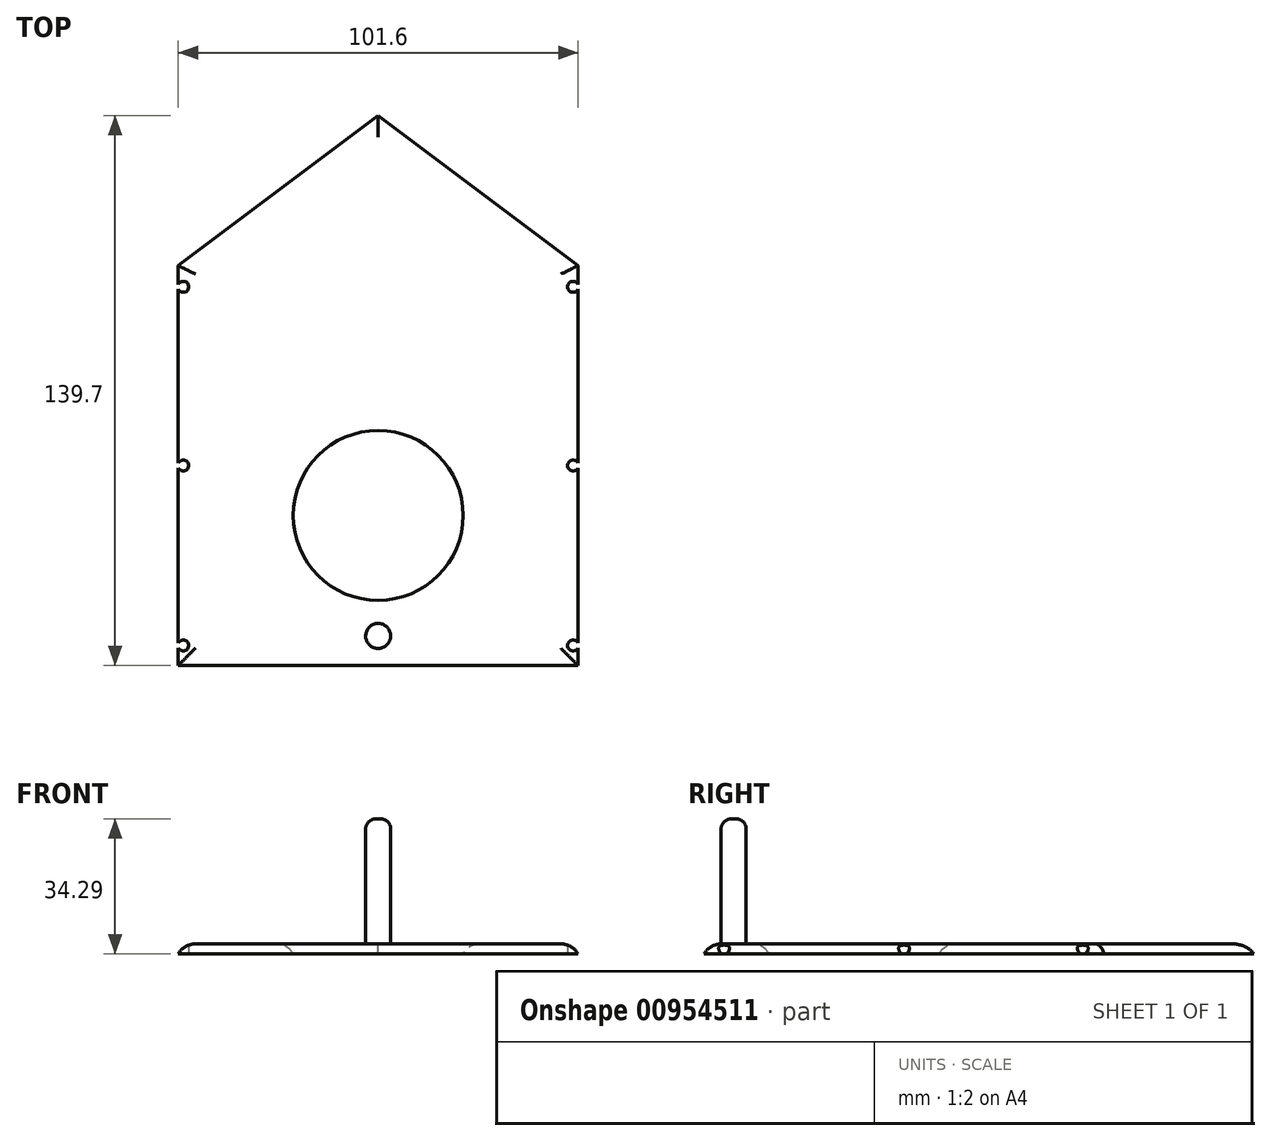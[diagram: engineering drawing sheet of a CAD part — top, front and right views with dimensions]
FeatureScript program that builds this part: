
annotation { "Feature Type Name" : "Feature", "Feature Type Description" : "" }
export const myFeature = defineFeature(function(context is Context, id is Id, definition is map)
    precondition{}
    {
        {
            var Q0;
            Q0=qCreatedBy(makeId("Top.planeOp"),FACE);
            var sketch = newSketch(context, id + "F0", { "sketchPlane" : qUnion([Q0])});
            skLineSegment(sketch, "E0.bottom", {"start": v(50.8, -50.8) * mm, "end": v(-50.8, -50.8) * mm});
            skLineSegment(sketch, "E0.top", {"start": v(50.8, 50.8) * mm, "end": v(-50.8, 50.8) * mm});
            skLineSegment(sketch, "E0.left", {"start": v(50.8, -50.8) * mm, "end": v(50.8, 50.8) * mm});
            skLineSegment(sketch, "E0.right", {"start": v(-50.8, -50.8) * mm, "end": v(-50.8, 50.8) * mm});
            skPoint(sketch, "E0.middle", {"position": v(0, 0) * mm});
            skLineSegment(sketch, "E1", {"start": v(-50.8, 50.8) * mm, "end": v(0, 88.9) * mm});
            skLineSegment(sketch, "E2", {"start": v(0, 88.9) * mm, "end": v(50.8, 50.8) * mm});
            skPoint(sketch, "E3", {"position": v(0, -12.7) * mm});
            skCircle(sketch, "E4", {"center": v(0, -12.7) * mm, "radius": 21.59 * mm});
            skSolve(sketch);
        }
        {
            var Q0;
            Q0 = qSketchRegion(id + "F0", true);
            extrude(context, id + "F1", {"entities" : qUnion([Q0]), "depth" : 2.54 * mm, "offsetDistance" : 25.4 * mm});
        }
        {
            var Q0;
            Q0=makeQuery(id+"F1.opExtrude","CAP_EDGE",EDGE,{"disambiguationData":[OSD([sQuery(id+"F0.wireOp",EDGE,"E4")])],"isStart":false});
            fillet(context, id + "F2", {"entities" : qUnion([Q0]), "radius" : 4.83 * mm, "tangentPropagation" : true, "allowEdgeOverflow" : false});
        }
        {
            var Q0;
            Q0=makeQuery(id+"F1.opExtrude","CAP_FACE",FACE,{"disambiguationData":[OSD([sQuery(id+"F0.wireOp",EDGE,"E0.bottom"),sQuery(id+"F0.wireOp",EDGE,"E0.left"),sQuery(id+"F0.wireOp",EDGE,"E0.right"),sQuery(id+"F0.wireOp",EDGE,"E1"),sQuery(id+"F0.wireOp",EDGE,"E2"),sQuery(id+"F0.wireOp",EDGE,"E4")])],"isStart":false});
            var sketch = newSketch(context, id + "F3", { "sketchPlane" : qUnion([Q0])});
            skPoint(sketch, "E5", {"position": v(0, -43.3) * mm});
            skCircle(sketch, "E6", {"center": v(0, -43.3) * mm, "radius": 3.18 * mm});
            skSolve(sketch);
        }
        {
            var Q0;
            Q0=makeQuery(id+"F3.imprint","IMPRINT",FACE,{"disambiguationData":[TD([[makeQuery(id+"F3.imprint","IMPRINT",EDGE,{"derivedFrom":sQuery(id+"F3.wireOp",EDGE,"E6")}),1.0]])]});
            extrude(context, id + "F4", {"entities" : qUnion([Q0]), "operationType" : NewBodyOperationType.ADD, "depth" : 31.75 * mm, "offsetDistance" : 25.4 * mm});
        }
        {
            var Q0;
            Q0=makeQuery(id+"F4.opExtrude","CAP_EDGE",EDGE,{"disambiguationData":[OSD([sQuery(id+"F3.wireOp",EDGE,"E6")])],"isStart":false});
            fillet(context, id + "F5", {"entities" : qUnion([Q0]), "radius" : 2.54 * mm, "tangentPropagation" : true, "allowEdgeOverflow" : false});
        }
        {
            var Q0;
            Q0=makeQuery(id+"F1.opExtrude","CAP_EDGE",EDGE,{"disambiguationData":[OSD([sQuery(id+"F0.wireOp",EDGE,"E0.bottom")])],"isStart":false});
            var Q1;
            Q1=makeQuery(id+"F1.opExtrude","CAP_EDGE",EDGE,{"disambiguationData":[OSD([sQuery(id+"F0.wireOp",EDGE,"E0.left")])],"isStart":false});
            var Q2;
            Q2=makeQuery(id+"F1.opExtrude","CAP_EDGE",EDGE,{"disambiguationData":[OSD([sQuery(id+"F0.wireOp",EDGE,"E0.right")])],"isStart":false});
            var Q3;
            Q3=makeQuery(id+"F1.opExtrude","CAP_EDGE",EDGE,{"disambiguationData":[OSD([sQuery(id+"F0.wireOp",EDGE,"E1")])],"isStart":false});
            var Q4;
            Q4=makeQuery(id+"F1.opExtrude","CAP_EDGE",EDGE,{"disambiguationData":[OSD([sQuery(id+"F0.wireOp",EDGE,"E2")])],"isStart":false});
            fillet(context, id + "F6", {"entities" : qUnion([Q0, Q1, Q2, Q3, Q4]), "radius" : 5.08 * mm, "tangentPropagation" : true, "allowEdgeOverflow" : false});
        }
        {
            var Q0;
            Q0=makeQuery(id+"F0.imprint","IMPRINT",FACE,{"disambiguationData":[TD([[makeQuery(id+"F0.imprint","IMPRINT",EDGE,{"derivedFrom":sQuery(id+"F0.wireOp",EDGE,"E0.bottom")}),-1.0]])]});
            var sketch = newSketch(context, id + "F7", { "sketchPlane" : qUnion([Q0])});
            skPoint(sketch, "E7", {"position": v(49.53, 45.4) * mm});
            skPoint(sketch, "E8", {"position": v(49.53, 0) * mm});
            skPoint(sketch, "E9", {"position": v(49.53, -45.72) * mm});
            skPoint(sketch, "E10", {"position": v(-49.53, 45.4) * mm});
            skPoint(sketch, "E11", {"position": v(-49.53, 0) * mm});
            skPoint(sketch, "E12", {"position": v(-49.53, -45.72) * mm});
            skSolve(sketch);
        }
        {
            var Q0;
            Q0=sQuery(id+"F7.wireOp",VERTEX,"E10");
            var Q1;
            Q1=sQuery(id+"F7.wireOp",VERTEX,"E11");
            var Q2;
            Q2=sQuery(id+"F7.wireOp",VERTEX,"E12");
            var Q3;
            Q3=sQuery(id+"F7.wireOp",VERTEX,"E9");
            var Q4;
            Q4=sQuery(id+"F7.wireOp",VERTEX,"E8");
            var Q5;
            Q5=sQuery(id+"F7.wireOp",VERTEX,"E7");
            var Q6;
            Q6=makeQuery(id+"F1.opExtrude","SWEPT_BODY",BODY,{"disambiguationData":[OSD([sQuery(id+"F0.wireOp",EDGE,"E0.bottom"),sQuery(id+"F0.wireOp",EDGE,"E0.left"),sQuery(id+"F0.wireOp",EDGE,"E0.right"),sQuery(id+"F0.wireOp",EDGE,"E1"),sQuery(id+"F0.wireOp",EDGE,"E2"),sQuery(id+"F0.wireOp",EDGE,"E4")])]});
            hole(context, id + "F8", {"style" : HoleStyle.SIMPLE, "endStyle" : HoleEndStyle.THROUGH, "oppositeDirection" : true, "holeDiameter" : 2.8 * mm, "majorDiameter" : 6.35 * mm, "isTappedThrough" : true, "tappedDepth" : 12.7 * mm, "tapClearance" : 3, "locations" : qUnion([Q0, Q1, Q2, Q3, Q4, Q5]), "scope" : qUnion([Q6])});
        }
    });
